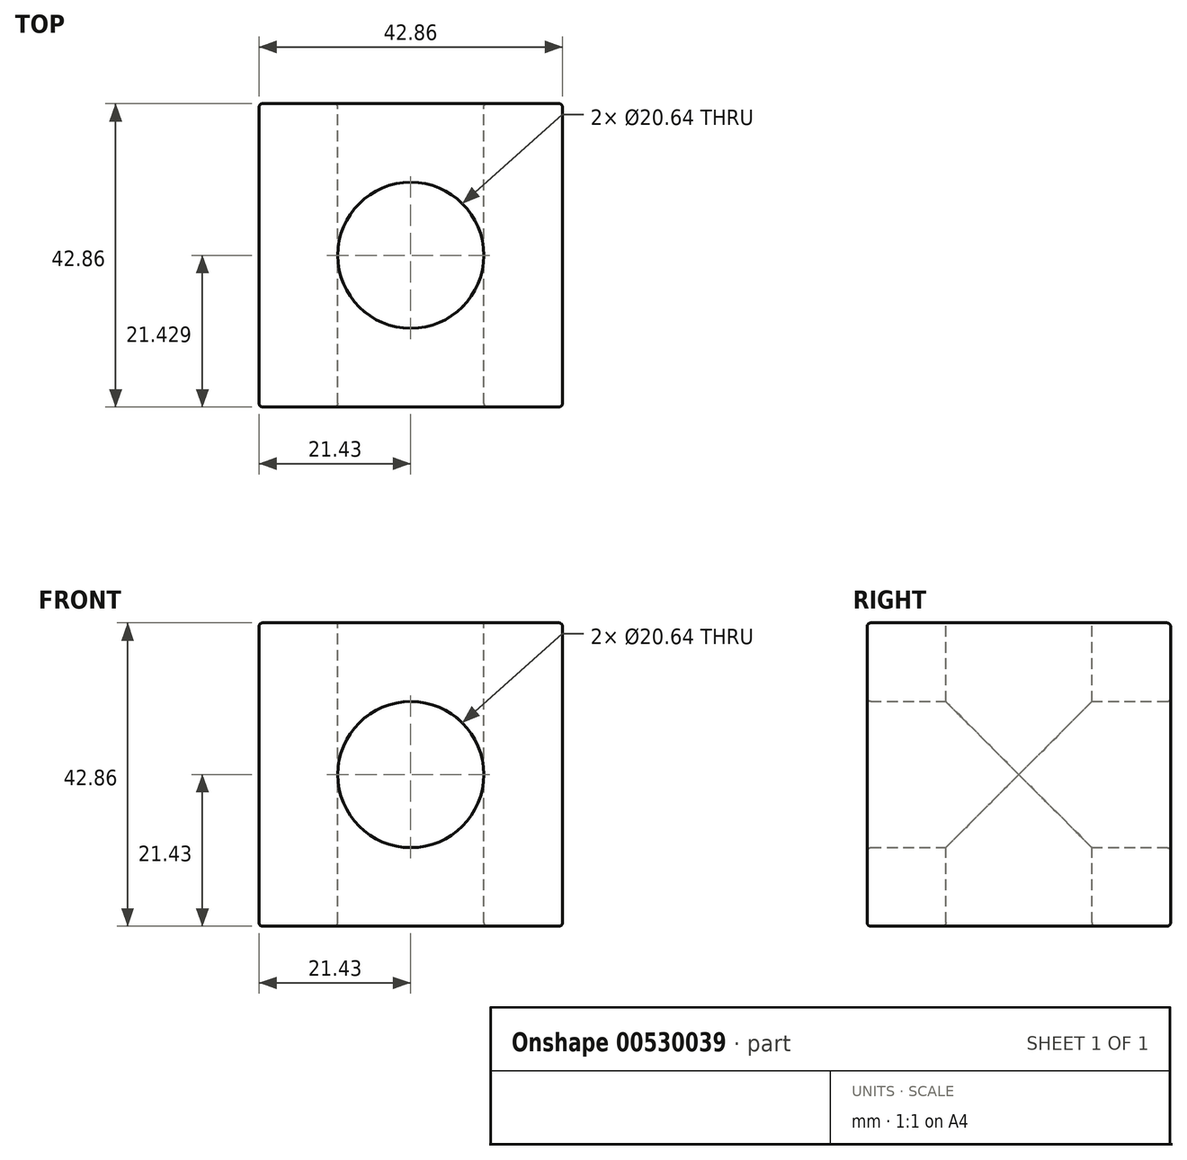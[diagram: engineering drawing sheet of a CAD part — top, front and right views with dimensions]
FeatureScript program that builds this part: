
annotation { "Feature Type Name" : "Feature", "Feature Type Description" : "" }
export const myFeature = defineFeature(function(context is Context, id is Id, definition is map)
    precondition{}
    {
        {
            var Q0;
            Q0=qCreatedBy(makeId("Front.planeOp"),FACE);
            var sketch = newSketch(context, id + "F0", { "sketchPlane" : qUnion([Q0])});
            skLineSegment(sketch, "E0.bottom", {"start": v(21.43, 21.43) * mm, "end": v(-21.43, 21.43) * mm});
            skLineSegment(sketch, "E0.top", {"start": v(21.43, -21.43) * mm, "end": v(-21.43, -21.43) * mm});
            skLineSegment(sketch, "E0.left", {"start": v(21.43, 21.43) * mm, "end": v(21.43, -21.43) * mm});
            skLineSegment(sketch, "E0.right", {"start": v(-21.43, 21.43) * mm, "end": v(-21.43, -21.43) * mm});
            skPoint(sketch, "E0.middle", {"position": v(0, 0) * mm});
            skCircle(sketch, "E1", {"center": v(0, 0) * mm, "radius": 10.32 * mm});
            skSolve(sketch);
        }
        {
            var Q0;
            Q0=qSketchRegion(id+"F0",true);
            extrude(context, id + "F1", {"entities" : qUnion([Q0]), "depth" : 42.86 * mm});
        }
        {
            var Q0;
            Q0=makeQuery(id+"F1.opExtrude","SWEPT_FACE",FACE,{"disambiguationData":[OSD([sQuery(id+"F0.wireOp",EDGE,"E0.bottom")])]});
            var sketch = newSketch(context, id + "F2", { "sketchPlane" : qUnion([Q0])});
            skCircle(sketch, "E2", {"center": v(0, -21.43) * mm, "radius": 10.32 * mm});
            skSolve(sketch);
        }
        {
            var Q0;
            Q0=qSketchRegion(id+"F2",true);
            extrude(context, id + "F3", {"entities" : qUnion([Q0]), "operationType" : NewBodyOperationType.REMOVE, "endBound" : BoundingType.THROUGH_ALL, "oppositeDirection" : true, "depth" : 42.93 * mm});
        }
        {
            var Q0;
            Q0=makeQuery(id+"F1.opExtrude","CAP_EDGE",EDGE,{"disambiguationData":[OSD([sQuery(id+"F0.wireOp",EDGE,"E0.bottom")])],"isStart":false});
            fillet(context, id + "F4", {"entities" : qUnion([Q0]), "radius" : 0.5 * mm, "tangentPropagation" : true, "allowEdgeOverflow" : false});
        }
        {
            var Q0;
            Q0=makeQuery(id+"F1.opExtrude","SWEPT_EDGE",EDGE,{"disambiguationData":[OSD([sQuery(id+"F0.wireOp",EDGE,"E0.bottom"),sQuery(id+"F0.wireOp",EDGE,"E0.left")])]});
            var Q1;
            Q1=makeQuery(id+"F1.opExtrude","CAP_EDGE",EDGE,{"disambiguationData":[OSD([sQuery(id+"F0.wireOp",EDGE,"E0.left")])],"isStart":true});
            var Q2;
            Q2=makeQuery(id+"F1.opExtrude","SWEPT_EDGE",EDGE,{"disambiguationData":[OSD([sQuery(id+"F0.wireOp",EDGE,"E0.top"),sQuery(id+"F0.wireOp",EDGE,"E0.left")])]});
            var Q3;
            Q3=makeQuery(id+"F1.opExtrude","CAP_EDGE",EDGE,{"disambiguationData":[OSD([sQuery(id+"F0.wireOp",EDGE,"E0.right")])],"isStart":false});
            var Q4;
            Q4=makeQuery(id+"F1.opExtrude","CAP_EDGE",EDGE,{"disambiguationData":[OSD([sQuery(id+"F0.wireOp",EDGE,"E0.top")])],"isStart":false});
            var Q5;
            Q5=makeQuery(id+"F1.opExtrude","CAP_EDGE",EDGE,{"disambiguationData":[OSD([sQuery(id+"F0.wireOp",EDGE,"E0.top")])],"isStart":true});
            var Q6;
            Q6=makeQuery(id+"F1.opExtrude","SWEPT_EDGE",EDGE,{"disambiguationData":[OSD([sQuery(id+"F0.wireOp",EDGE,"E0.top"),sQuery(id+"F0.wireOp",EDGE,"E0.right")])]});
            var Q7;
            Q7=makeQuery(id+"F1.opExtrude","CAP_EDGE",EDGE,{"disambiguationData":[OSD([sQuery(id+"F0.wireOp",EDGE,"E0.bottom")])],"isStart":true});
            var Q8;
            Q8=makeQuery(id+"F1.opExtrude","CAP_EDGE",EDGE,{"disambiguationData":[OSD([sQuery(id+"F0.wireOp",EDGE,"E0.left")])],"isStart":false});
            var Q9;
            {var subQ0=sQuery(id+"F0.wireOp",EDGE,"E0.bottom");Q9=makeQuery(id+"F4.opFillet","BLEND_EDGE",EDGE,{"blendedFrom":[makeQuery(id+"F1.opExtrude","CAP_EDGE",EDGE,{"disambiguationData":[OSD([subQ0])],"isStart":false}),makeQuery(id+"F1.opExtrude","CAP_FACE",FACE,{"disambiguationData":[OSD([subQ0,sQuery(id+"F0.wireOp",EDGE,"E0.top"),sQuery(id+"F0.wireOp",EDGE,"E0.left"),sQuery(id+"F0.wireOp",EDGE,"E0.right"),sQuery(id+"F0.wireOp",EDGE,"E1")])],"isStart":false})],"blendedInto":[makeQuery(id+"F1.opExtrude","CAP_FACE",FACE,{"disambiguationData":[OSD([subQ0,sQuery(id+"F0.wireOp",EDGE,"E0.top"),sQuery(id+"F0.wireOp",EDGE,"E0.left"),sQuery(id+"F0.wireOp",EDGE,"E0.right"),sQuery(id+"F0.wireOp",EDGE,"E1")])],"isStart":false})]});}
            var Q10;
            Q10=makeQuery(id+"F1.opExtrude","CAP_EDGE",EDGE,{"disambiguationData":[OSD([sQuery(id+"F0.wireOp",EDGE,"E0.right")])],"isStart":true});
            var Q11;
            Q11=makeQuery(id+"F1.opExtrude","SWEPT_EDGE",EDGE,{"disambiguationData":[OSD([sQuery(id+"F0.wireOp",EDGE,"E0.bottom"),sQuery(id+"F0.wireOp",EDGE,"E0.right")])]});
            fillet(context, id + "F5", {"entities" : qUnion([Q0, Q1, Q2, Q3, Q4, Q5, Q6, Q7, Q8, Q9, Q10, Q11]), "radius" : 0.5 * mm, "tangentPropagation" : true, "allowEdgeOverflow" : false});
        }
        {
            var Q0;
            Q0=makeQuery(id+"F1.opExtrude","CAP_EDGE",EDGE,{"disambiguationData":[OSD([sQuery(id+"F0.wireOp",EDGE,"E1")])],"isStart":false});
            var Q1;
            Q1=makeQuery(id+"F3.boolean.opBoolean","INTERSECT",EDGE,{"derivedFrom":[makeQuery(id+"F1.opExtrude","SWEPT_FACE",FACE,{"disambiguationData":[OSD([sQuery(id+"F0.wireOp",EDGE,"E0.top")])]}),makeQuery(id+"F3.opExtrude","SWEPT_FACE",FACE,{"disambiguationData":[OSD([sQuery(id+"F2.wireOp",EDGE,"E2")])]})]});
            var Q2;
            Q2=makeQuery(id+"F3.boolean.opBoolean","COPY",EDGE,{"derivedFrom":makeQuery(id+"F3.opExtrude","CAP_EDGE",EDGE,{"disambiguationData":[OSD([sQuery(id+"F2.wireOp",EDGE,"E2")])],"isStart":true})});
            var Q3;
            Q3=makeQuery(id+"F1.opExtrude","CAP_EDGE",EDGE,{"disambiguationData":[OSD([sQuery(id+"F0.wireOp",EDGE,"E1")])],"isStart":true});
            fillet(context, id + "F6", {"entities" : qUnion([Q0, Q1, Q2, Q3]), "radius" : 0.5 * mm, "tangentPropagation" : true, "allowEdgeOverflow" : false});
        }
    });
